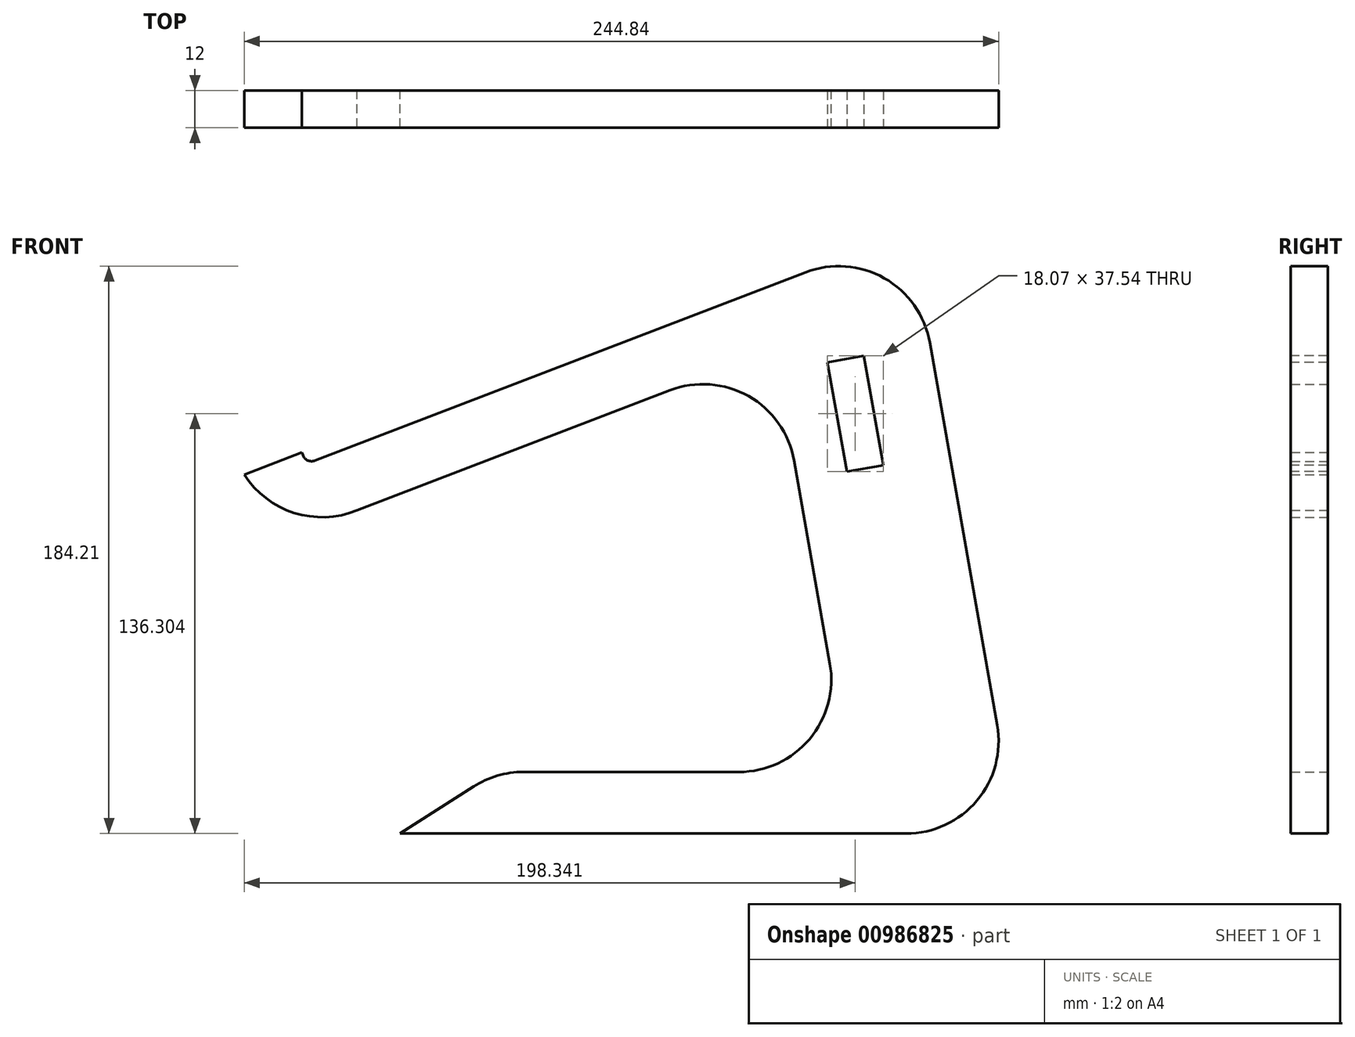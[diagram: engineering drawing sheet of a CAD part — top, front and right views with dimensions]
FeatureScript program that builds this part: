
annotation { "Feature Type Name" : "Feature", "Feature Type Description" : "" }
export const myFeature = defineFeature(function(context is Context, id is Id, definition is map)
    precondition{}
    {
        {
            var Q0;
            Q0=qCreatedBy(makeId("Front.planeOp"),FACE);
            var sketch = newSketch(context, id + "F0", { "sketchPlane" : qUnion([Q0])});
            skLineSegment(sketch, "E0", {"start": v(-177.62, 123.73) * mm, "end": v(-177.26, 122.8) * mm});
            skLineSegment(sketch, "E1", {"start": v(-173.38, 121.08) * mm, "end": v(-14.1, 182.22) * mm});
            skLineSegment(sketch, "E2", {"start": v(26.19, 159.42) * mm, "end": v(48.09, 35.2) * mm});
            skLineSegment(sketch, "E3", {"start": v(18.55, 0) * mm, "end": v(-145.7, 0) * mm});
            skLineSegment(sketch, "E4", {"start": v(-145.7, 0) * mm, "end": v(-121.89, 15.26) * mm});
            skLineSegment(sketch, "E5", {"start": v(-105.7, 20) * mm, "end": v(-35.75, 20) * mm});
            skLineSegment(sketch, "E6", {"start": v(-6.2, 55.2) * mm, "end": v(-17.83, 121.1) * mm});
            skLineSegment(sketch, "E7", {"start": v(-58.12, 143.9) * mm, "end": v(-159.68, 104.91) * mm});
            skPoint(sketch, "E8.visualSharp", {"position": v(-114.49, 20) * mm});
            skArc(sketch, "E8.filletArc", {"start": v(-105.7, 20) * mm, "mid": v(-114.13, 18.8) * mm, "end": v(-121.89, 15.26) * mm});
            skPoint(sketch, "E9.visualSharp", {"position": v(54.3, 0) * mm});
            skArc(sketch, "E9.filletArc", {"start": v(18.55, 0) * mm, "mid": v(41.53, 10.72) * mm, "end": v(48.09, 35.2) * mm});
            skPoint(sketch, "E10.visualSharp", {"position": v(0, 20) * mm});
            skArc(sketch, "E10.filletArc", {"start": v(-35.75, 20) * mm, "mid": v(-12.77, 30.72) * mm, "end": v(-6.2, 55.2) * mm});
            skPoint(sketch, "E11.visualSharp", {"position": v(-24.15, 156.94) * mm});
            skArc(sketch, "E11.filletArc", {"start": v(-17.83, 121.1) * mm, "mid": v(-32.6, 142) * mm, "end": v(-58.12, 143.9) * mm});
            skPoint(sketch, "E12.visualSharp", {"position": v(19.87, 195.26) * mm});
            skArc(sketch, "E12.filletArc", {"start": v(26.19, 159.42) * mm, "mid": v(11.42, 180.32) * mm, "end": v(-14.1, 182.22) * mm});
            skPoint(sketch, "E13.visualSharp", {"position": v(-187.69, 94.16) * mm});
            skPoint(sketch, "E14.visualSharp", {"position": v(-176.18, 120) * mm});
            skArc(sketch, "E14.filletArc", {"start": v(-177.26, 122.8) * mm, "mid": v(-175.68, 121.14) * mm, "end": v(-173.38, 121.08) * mm});
            skLineSegment(sketch, "E15", {"start": v(-196.29, 116.57) * mm, "end": v(-177.62, 123.73) * mm});
            skArc(sketch, "E16", {"start": v(-196.29, 116.57) * mm, "mid": v(-180.1, 104.11) * mm, "end": v(-159.68, 104.91) * mm});
            skSolve(sketch);
        }
        {
            var Q0;
            Q0 = qSketchRegion(id + "F0", true);
            extrude(context, id + "F1", {"entities" : qUnion([Q0]), "depth" : 12 * mm, "offsetDistance" : 25 * mm});
        }
        {
            var Q0;
            Q0=makeQuery(id+"F1.opExtrude","CAP_FACE",FACE,{"disambiguationData":[OSD([sQuery(id+"F0.wireOp",EDGE,"E0"),sQuery(id+"F0.wireOp",EDGE,"E1"),sQuery(id+"F0.wireOp",EDGE,"E2"),sQuery(id+"F0.wireOp",EDGE,"E3"),sQuery(id+"F0.wireOp",EDGE,"E4"),sQuery(id+"F0.wireOp",EDGE,"E5"),sQuery(id+"F0.wireOp",EDGE,"E6"),sQuery(id+"F0.wireOp",EDGE,"E7"),sQuery(id+"F0.wireOp",EDGE,"E8.filletArc"),sQuery(id+"F0.wireOp",EDGE,"E9.filletArc"),sQuery(id+"F0.wireOp",EDGE,"E10.filletArc"),sQuery(id+"F0.wireOp",EDGE,"E11.filletArc"),sQuery(id+"F0.wireOp",EDGE,"E12.filletArc"),sQuery(id+"F0.wireOp",EDGE,"E14.filletArc"),sQuery(id+"F0.wireOp",EDGE,"E15"),sQuery(id+"F0.wireOp",EDGE,"E16")])],"isStart":false});
            var sketch = newSketch(context, id + "F2", { "sketchPlane" : qUnion([Q0])});
            skLineSegment(sketch, "E17.bottom", {"start": v(-6.98, 152.99) * mm, "end": v(4.83, 155.07) * mm});
            skLineSegment(sketch, "E17.top", {"start": v(-0.73, 117.54) * mm, "end": v(11.09, 119.62) * mm});
            skLineSegment(sketch, "E17.left", {"start": v(-6.98, 152.99) * mm, "end": v(-0.73, 117.54) * mm});
            skLineSegment(sketch, "E17.right", {"start": v(4.83, 155.07) * mm, "end": v(11.09, 119.62) * mm});
            skSolve(sketch);
        }
        {
            var Q0;
            Q0 = qSketchRegion(id + "F2", true);
            extrude(context, id + "F3", {"entities" : qUnion([Q0]), "operationType" : NewBodyOperationType.REMOVE, "endBound" : BoundingType.THROUGH_ALL, "oppositeDirection" : true, "depth" : 25 * mm, "offsetDistance" : 25 * mm});
        }
    });
